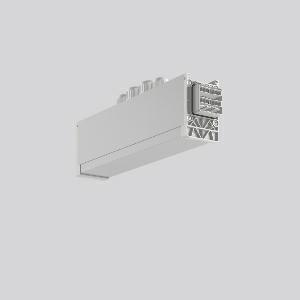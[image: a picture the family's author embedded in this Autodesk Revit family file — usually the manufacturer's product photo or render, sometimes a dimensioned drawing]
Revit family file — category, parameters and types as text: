
# Revit family: linedo_mitteleinspeisung_7pol_982698_010_3_0258
name_source: partatom
category: Lighting Fixtures
units: mm (PartAtom-declared; Revit-internal decimal feet)

## family parameters
Cut with Voids When Loaded = No
Host = Face
Light Source = No
Part Type = Normal
Room Calculation Point = No
Round Connector Dimension = Use Diameter
Shared = No

## types (1)
- LINEDO_Mitteleinspeisung_7pol
    Apparent Load = 0 VA
    Default Elevation = 1800 mm
    Description = Series: LINEDO
Middle power feed, 7-pole, connection socket / plug. Housing: extruded aluminium profile, anodised. Cover made of plastic, surface like housing. LINEDO plug system, plastic, light grey. 4 cable glands (2 x M20 and 2 x M25). Cable glands on top. Easy connection for rigid or flexible wires. Especially for use with continuous line modules with high opal diffuser.
Colour: anodised aluminium
Length: 330 mm
Width: 58 mm
Height: 91 mm
Weight: 801 g
    Height = 91 mm
    Lamp = 0 x
    Length = 330 mm
    Luminous efficacy = 0 lm/W
    Manufacturer = RZB
    ModVariant = No
    Model = 982698.010.3
    Mounting Place = Ceiling
    Mounting Type = Surface mounted
    Number of Poles = 1
    OnlyDefault = Yes
    Power Factor = 1
    Product Name = LINEDO_Mitteleinspeisung_7pol
    Product group = Surface mounted continuous line luminaire system
    ProductGroupID = 310
    Protection Class = Protection class I
    Protection Degree = Degree of protection
    RLX_Detail_Level = 1
    RLX_Emergency_Light_Flux = 0 lm
    RLX_Emergency_Type = 0
    RLX_Emergency_Type_DB = No
    RlxData = <blob elided: 23089 chars, md5=2c82fd14>
    Standby Power = 0 W
    System Light Flux = 0 lm
    System Power = 0 W
    Type Comments = Product without accessories
    Type Image = 982698.010.jpg
    URL = http://relux.com
    VarID = ---
    Voltage = 0 V
    Weight = 0.00 kg
    Width = 58 mm

## geometry (parser evidence)
native form markers: Blend x4, Sweep x13
no freeform markers — native parametric forms only
